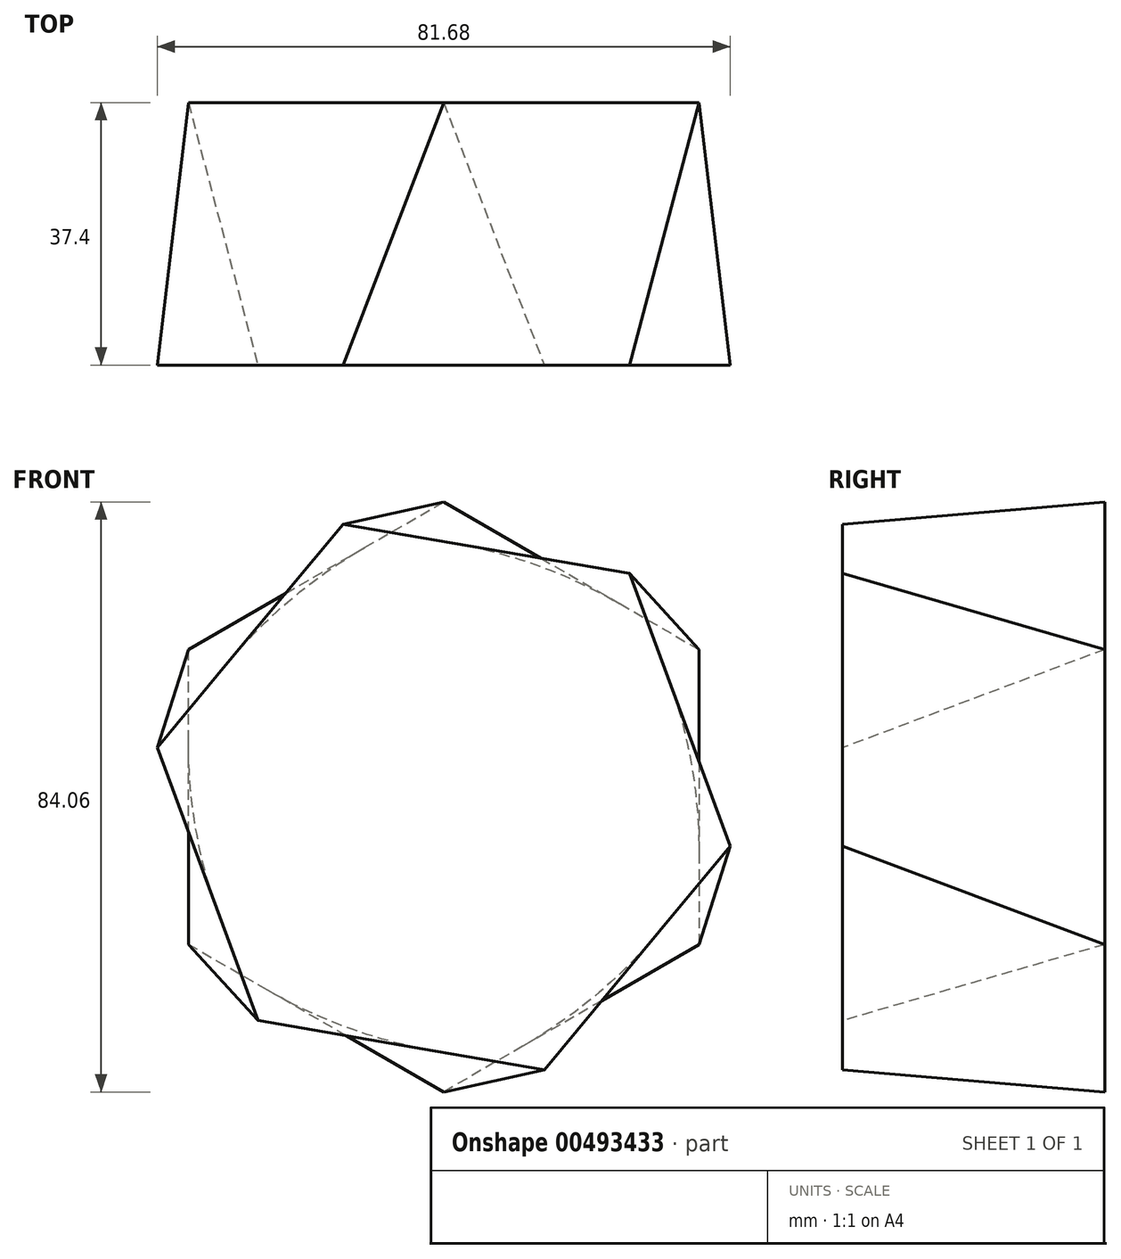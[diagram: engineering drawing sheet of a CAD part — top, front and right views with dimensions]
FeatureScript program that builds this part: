
annotation { "Feature Type Name" : "Feature", "Feature Type Description" : "" }
export const myFeature = defineFeature(function(context is Context, id is Id, definition is map)
    precondition{}
    {
        {
            var Q0;
            Q0=qCreatedBy(makeId("Front.planeOp"),FACE);
            var sketch = newSketch(context, id + "F0", { "sketchPlane" : qUnion([Q0])});
            skCircle(sketch, "E0.cCircle", {"center": v(0, 0) * mm, "radius": 42.03 * mm, "construction": true});
            skLineSegment(sketch, "E0.0", {"start": v(0, 42.03) * mm, "end": v(36.4, 21.01) * mm});
            skLineSegment(sketch, "E0.1", {"start": v(36.4, 21.01) * mm, "end": v(36.4, -21.01) * mm});
            skLineSegment(sketch, "E0.2", {"start": v(36.4, -21.01) * mm, "end": v(0, -42.03) * mm});
            skLineSegment(sketch, "E0.3", {"start": v(0, -42.03) * mm, "end": v(-36.4, -21.01) * mm});
            skLineSegment(sketch, "E0.4", {"start": v(-36.4, -21.01) * mm, "end": v(-36.4, 21.01) * mm});
            skLineSegment(sketch, "E0.5", {"start": v(-36.4, 21.01) * mm, "end": v(0, 42.03) * mm});
            skSolve(sketch);
        }
        {
            var Q0;
            Q0=qCreatedBy(makeId("Front.planeOp"),FACE);
            cPlane(context, id + "F1", {"entities" : qUnion([Q0]), "cplaneType" : CPlaneType.OFFSET, "offset" : 37.4 * mm, "width" : 150 * mm, "height" : 150 * mm});
        }
        {
            var Q0;
            Q0=qCreatedBy(id+"F1.planeOp",FACE);
            var sketch = newSketch(context, id + "F2", { "sketchPlane" : qUnion([Q0])});
            skCircle(sketch, "E1.cCircle", {"center": v(0, 0) * mm, "radius": 41.44 * mm, "construction": true});
            skLineSegment(sketch, "E1.0", {"start": v(-14.34, 38.87) * mm, "end": v(26.5, 31.86) * mm});
            skLineSegment(sketch, "E1.1", {"start": v(26.5, 31.86) * mm, "end": v(40.84, -7.01) * mm});
            skLineSegment(sketch, "E1.2", {"start": v(40.84, -7.01) * mm, "end": v(14.34, -38.87) * mm});
            skLineSegment(sketch, "E1.3", {"start": v(14.34, -38.87) * mm, "end": v(-26.5, -31.86) * mm});
            skLineSegment(sketch, "E1.4", {"start": v(-26.5, -31.86) * mm, "end": v(-40.84, 7.01) * mm});
            skLineSegment(sketch, "E1.5", {"start": v(-40.84, 7.01) * mm, "end": v(-14.34, 38.87) * mm});
            skSolve(sketch);
        }
        {
            var Q0;
            Q0=makeQuery(id+"F0.imprint","IMPRINT",FACE,{"disambiguationData":[TD([[makeQuery(id+"F0.imprint","IMPRINT",EDGE,{"derivedFrom":sQuery(id+"F0.wireOp",EDGE,"E0.0")}),-1.0]])]});
            var Q1;
            Q1=makeQuery(id+"F2.imprint","IMPRINT",FACE,{"disambiguationData":[TD([[makeQuery(id+"F2.imprint","IMPRINT",EDGE,{"derivedFrom":sQuery(id+"F2.wireOp",EDGE,"E1.0")}),-1.0]])]});
            loft(context, id + "F3", {"sheetProfilesArray" : [{ "sheetProfileEntities" : qUnion([Q0]) }, { "sheetProfileEntities" : qUnion([Q1]) }]});
        }
    });
